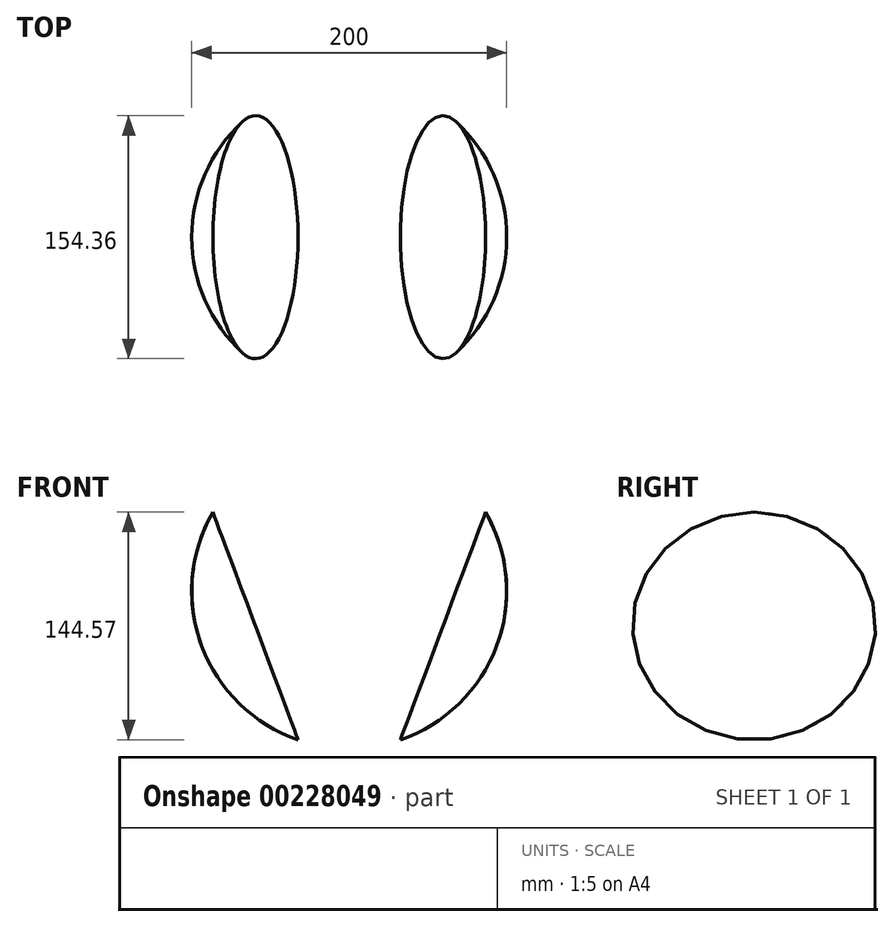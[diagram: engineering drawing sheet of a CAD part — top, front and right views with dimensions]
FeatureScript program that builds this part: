
annotation { "Feature Type Name" : "Feature", "Feature Type Description" : "" }
export const myFeature = defineFeature(function(context is Context, id is Id, definition is map)
    precondition{}
    {
        {
            var Q0;
            Q0=qCreatedBy(makeId("Top.planeOp"),FACE);
            var sketch = newSketch(context, id + "F0", { "sketchPlane" : qUnion([Q0])});
            skCircle(sketch, "E0", {"center": v(0, 0) * mm, "radius": 100 * mm, "construction": true});
            skSolve(sketch);
        }
        {
            var Q0;
            Q0=qCreatedBy(makeId("Front.planeOp"),FACE);
            var sketch = newSketch(context, id + "F1", { "sketchPlane" : qUnion([Q0])});
            skCircle(sketch, "E1", {"center": v(0, 0) * mm, "radius": 100 * mm, "construction": true});
            skLineSegment(sketch, "E2", {"start": v(-86.6, 50) * mm, "end": v(86.6, 50) * mm, "construction": true});
            skLineSegment(sketch, "E3", {"start": v(-32.5, -94.57) * mm, "end": v(32.5, -94.57) * mm, "construction": true});
            skLineSegment(sketch, "E4", {"start": v(-86.6, 50) * mm, "end": v(-32.5, -94.57) * mm, "construction": true});
            skLineSegment(sketch, "E5", {"start": v(32.5, -94.57) * mm, "end": v(86.6, 50) * mm, "construction": true});
            skLineSegment(sketch, "E6", {"start": v(-59.55, -22.29) * mm, "end": v(-93.66, -35.05) * mm});
            skLineSegment(sketch, "E7", {"start": v(59.55, -22.29) * mm, "end": v(93.66, -35.05) * mm});
            skArc(sketch, "E8", {"start": v(86.6, 50) * mm, "mid": v(99.66, 8.27) * mm, "end": v(93.66, -35.05) * mm});
            skLineSegment(sketch, "E9", {"start": v(86.6, 50) * mm, "end": v(59.55, -22.29) * mm});
            skLineSegment(sketch, "E10", {"start": v(-59.55, -22.29) * mm, "end": v(-86.6, 50) * mm});
            skArc(sketch, "E11", {"start": v(-93.66, -35.05) * mm, "mid": v(-99.66, 8.27) * mm, "end": v(-86.6, 50) * mm});
            skSolve(sketch);
        }
        {
            var Q0;
            Q0=makeQuery(id+"F1.imprint","IMPRINT",FACE,{"disambiguationData":[TD([[makeQuery(id+"F1.imprint","IMPRINT",EDGE,{"derivedFrom":sQuery(id+"F1.wireOp",EDGE,"E7")}),1.0]])]});
            var Q1;
            Q1=sQuery(id+"F1.wireOp",EDGE,"E7");
            revolve(context, id + "F2", {"entities" : qUnion([Q0]), "axis" : qUnion([Q1]), "revolveType" : RevolveType.FULL});
        }
        {
            var Q0;
            Q0=makeQuery(id+"F1.imprint","IMPRINT",FACE,{"disambiguationData":[TD([[makeQuery(id+"F1.imprint","IMPRINT",EDGE,{"derivedFrom":sQuery(id+"F1.wireOp",EDGE,"E6")}),-1.0]])]});
            var Q1;
            Q1=sQuery(id+"F1.wireOp",EDGE,"E6");
            revolve(context, id + "F3", {"entities" : qUnion([Q0]), "axis" : qUnion([Q1]), "revolveType" : RevolveType.FULL});
        }
    });
